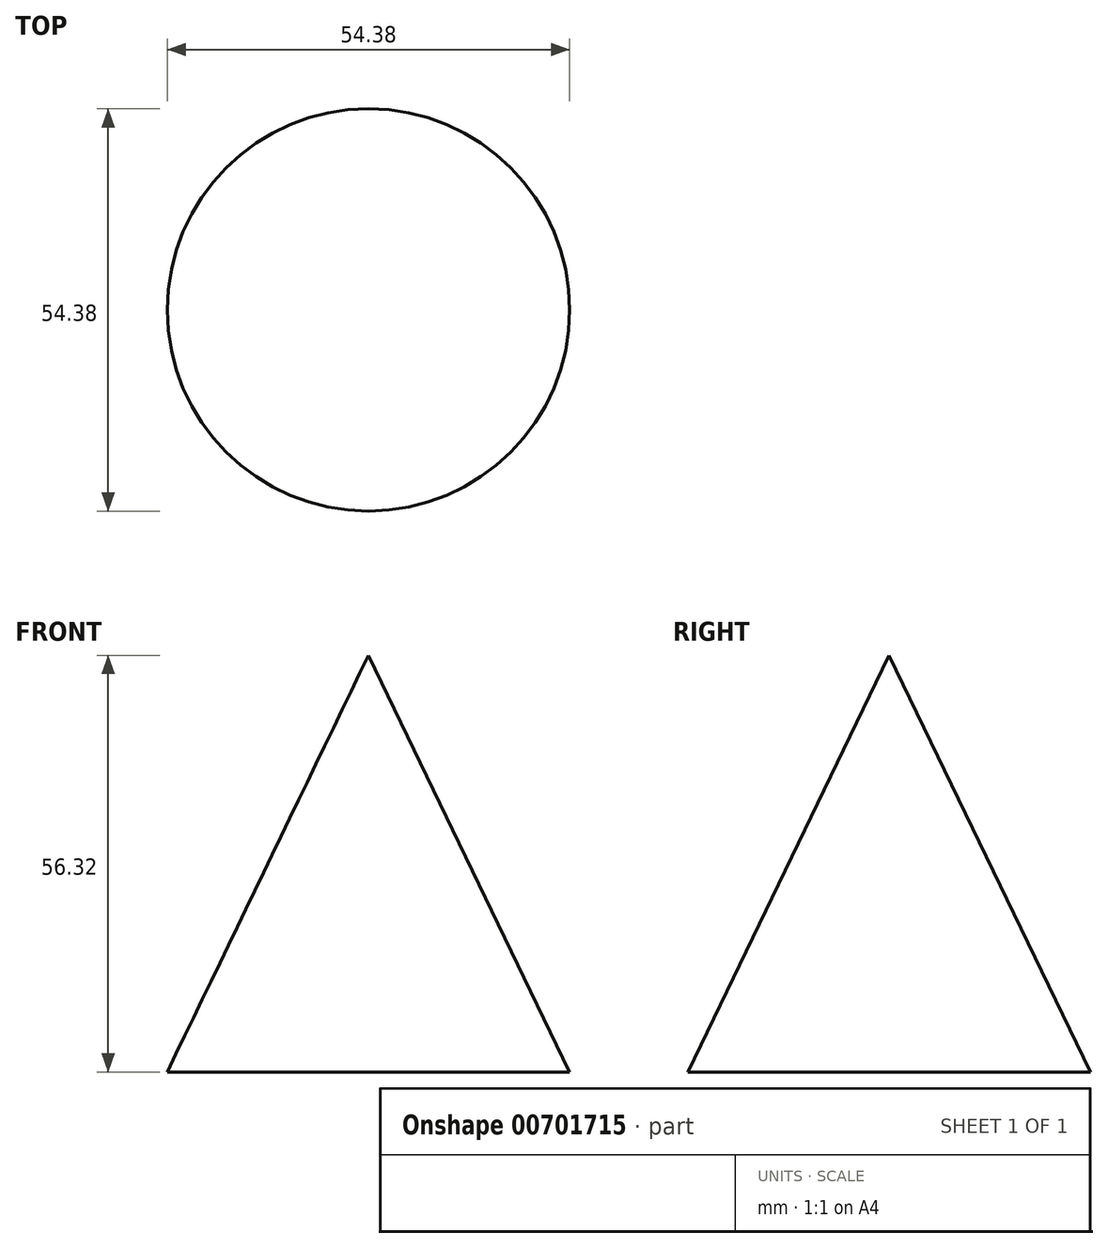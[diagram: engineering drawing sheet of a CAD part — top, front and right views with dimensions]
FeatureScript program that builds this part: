
annotation { "Feature Type Name" : "Feature", "Feature Type Description" : "" }
export const myFeature = defineFeature(function(context is Context, id is Id, definition is map)
    precondition{}
    {
        {
            var Q0;
            Q0=qCreatedBy(makeId("Front.planeOp"),FACE);
            var sketch = newSketch(context, id + "F0", { "sketchPlane" : qUnion([Q0])});
            skLineSegment(sketch, "E0", {"start": v(-27.2, 0) * mm, "end": v(0, 56.32) * mm});
            skLineSegment(sketch, "E1", {"start": v(-27.2, 0) * mm, "end": v(0, 0) * mm});
            skLineSegment(sketch, "E2", {"start": v(0, 0) * mm, "end": v(0, 56.32) * mm});
            skSolve(sketch);
        }
        {
            var Q0;
            Q0=sQuery(id+"F0.wireOp",EDGE,"E0");
            var Q1;
            Q1=sQuery(id+"F0.wireOp",EDGE,"E1");
            var Q2;
            Q2=sQuery(id+"F0.wireOp",EDGE,"E2");
            revolve(context, id + "F1", {"bodyType" : ToolBodyType.SURFACE, "surfaceOperationType" : NewSurfaceOperationType.NEW, "surfaceEntities" : qUnion([Q0, Q1]), "axis" : qUnion([Q2]), "revolveType" : RevolveType.FULL});
        }
    });
